# Revit family: 276079xx0--Acrylic shower tray with anti-slip base - Easy - Roca - 276079xx0
name_source: partatom
category: Generic Models
units: mm (PartAtom-declared; Revit-internal decimal feet)

## family parameters
Can host rebar = No
Cut with Voids When Loaded = No
Host = Face
Part Type = Normal
Room Calculation Point = No
Round Connector Dimension = Use Diameter
Shared = No

## types (2) — shared parameters
BIMobject category = Shower trays
Depth = 750.00
Description = Acrylic shower tray with anti-slip base
Design country = Spain
Drain diameter (mm) = 90 mm  [stored 0.295276 ft]
Eco green certification = No
Edition number = 1
Height = 60 mm
IFC Classification = Furnishing Element
Installation instructions = http://www.roca.com
Length = 750 mm
Manufacturer country = Spain
Manufacturer name = Roca
Manufacturer url = http://www.roca.com
Model = 276079..0
NBS Reference Code = 35-06-84
NBS Reference Description = Shower Trays
Nominal height = 65.00
Nominal width = 750.00
Product data url = http://roca.bimobject.com
Product family = Easy
Product group = Shower Tray
QR code = https://www.roca.com
Shape = Square
Suitable for Children = No
Suitable for Handicapped = No
Technical description = http://www.roca.com
UNSPSC Code = 301815
UNSPSC Name = Sanitary ware
URL = http://www.roca.com
Uniclass 1.4 Code = L72143
Uniclass 1.4 Description = Shower trays
Uniclass 2.0 Code = PR-35-06-84
Uniclass 2.0 Description = Shower Trays
Weight Net (Kg) = 0
Width = 750 mm
zero-valued in all types: Default Elevation

## per-type parameters (varying)
| type | Product SKU |
| White - Easy - Roca | A276079000 |
| Pergamon - Easy - Roca | A276079170 |

note: column(s) folded — value = type name in every type: Material

note: [stored X ft] marks values corroborated as IEEE doubles in the binary element streams (Revit-internal decimal feet)

## geometry (parser evidence)
native form markers: Blend x2, Sweep x1
no freeform markers — native parametric forms only
